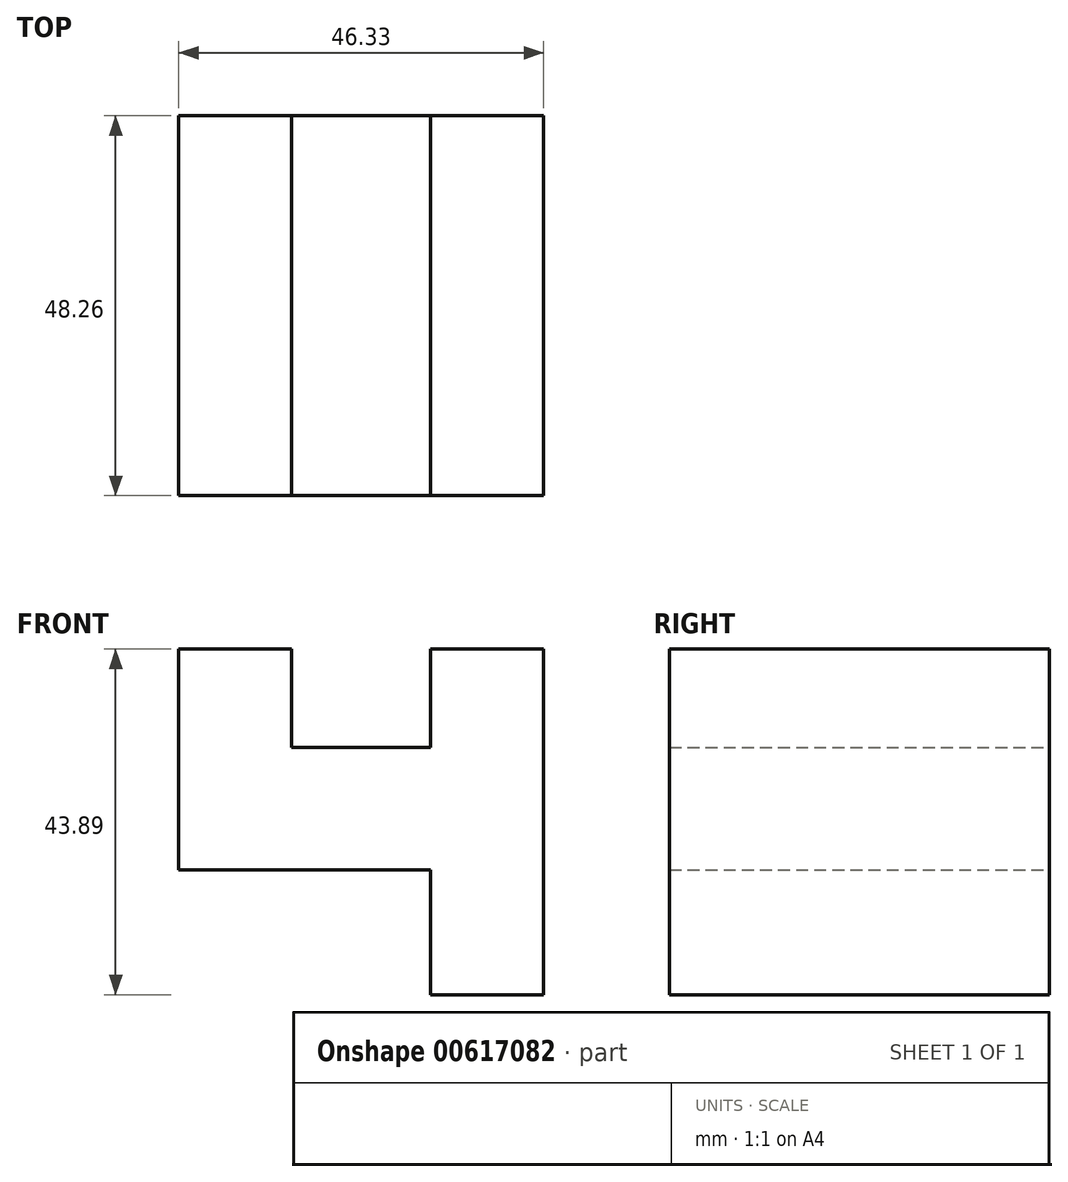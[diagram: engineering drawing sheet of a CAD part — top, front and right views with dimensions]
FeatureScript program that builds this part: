
annotation { "Feature Type Name" : "Feature", "Feature Type Description" : "" }
export const myFeature = defineFeature(function(context is Context, id is Id, definition is map)
    precondition{}
    {
        {
            var Q0;
            Q0=qCreatedBy(makeId("Front.planeOp"),FACE);
            var sketch = newSketch(context, id + "F0", { "sketchPlane" : qUnion([Q0])});
            skLineSegment(sketch, "E0", {"start": v(-43.13, 0) * mm, "end": v(-43.13, 12.5) * mm});
            skLineSegment(sketch, "E1", {"start": v(-43.13, 12.5) * mm, "end": v(-28.8, 12.5) * mm});
            skLineSegment(sketch, "E2", {"start": v(-28.8, 12.5) * mm, "end": v(-28.8, 0) * mm});
            skLineSegment(sketch, "E3", {"start": v(-28.8, 0) * mm, "end": v(-11.13, 0) * mm});
            skLineSegment(sketch, "E4", {"start": v(-11.13, 0) * mm, "end": v(-11.13, 12.5) * mm});
            skLineSegment(sketch, "E5", {"start": v(-11.13, 12.5) * mm, "end": v(3.2, 12.5) * mm});
            skLineSegment(sketch, "E6", {"start": v(3.2, 12.5) * mm, "end": v(3.2, 0) * mm});
            skLineSegment(sketch, "E7", {"start": v(3.2, 0) * mm, "end": v(3.2, -31.4) * mm});
            skLineSegment(sketch, "E8", {"start": v(3.2, -31.4) * mm, "end": v(-11.13, -31.4) * mm});
            skLineSegment(sketch, "E9", {"start": v(-11.13, -31.4) * mm, "end": v(-11.13, -15.54) * mm});
            skLineSegment(sketch, "E10", {"start": v(-11.13, -15.54) * mm, "end": v(-28.8, -15.54) * mm});
            skLineSegment(sketch, "E11", {"start": v(-28.8, -15.54) * mm, "end": v(-43.13, -15.54) * mm});
            skLineSegment(sketch, "E12", {"start": v(-43.13, 0) * mm, "end": v(-43.13, -15.54) * mm});
            skSolve(sketch);
        }
        {
            var Q0;
            Q0 = qSketchRegion(id + "F0", true);
            extrude(context, id + "F1", {"entities" : qUnion([Q0]), "depth" : 48.26 * mm, "offsetDistance" : 25.4 * mm});
        }
    });
